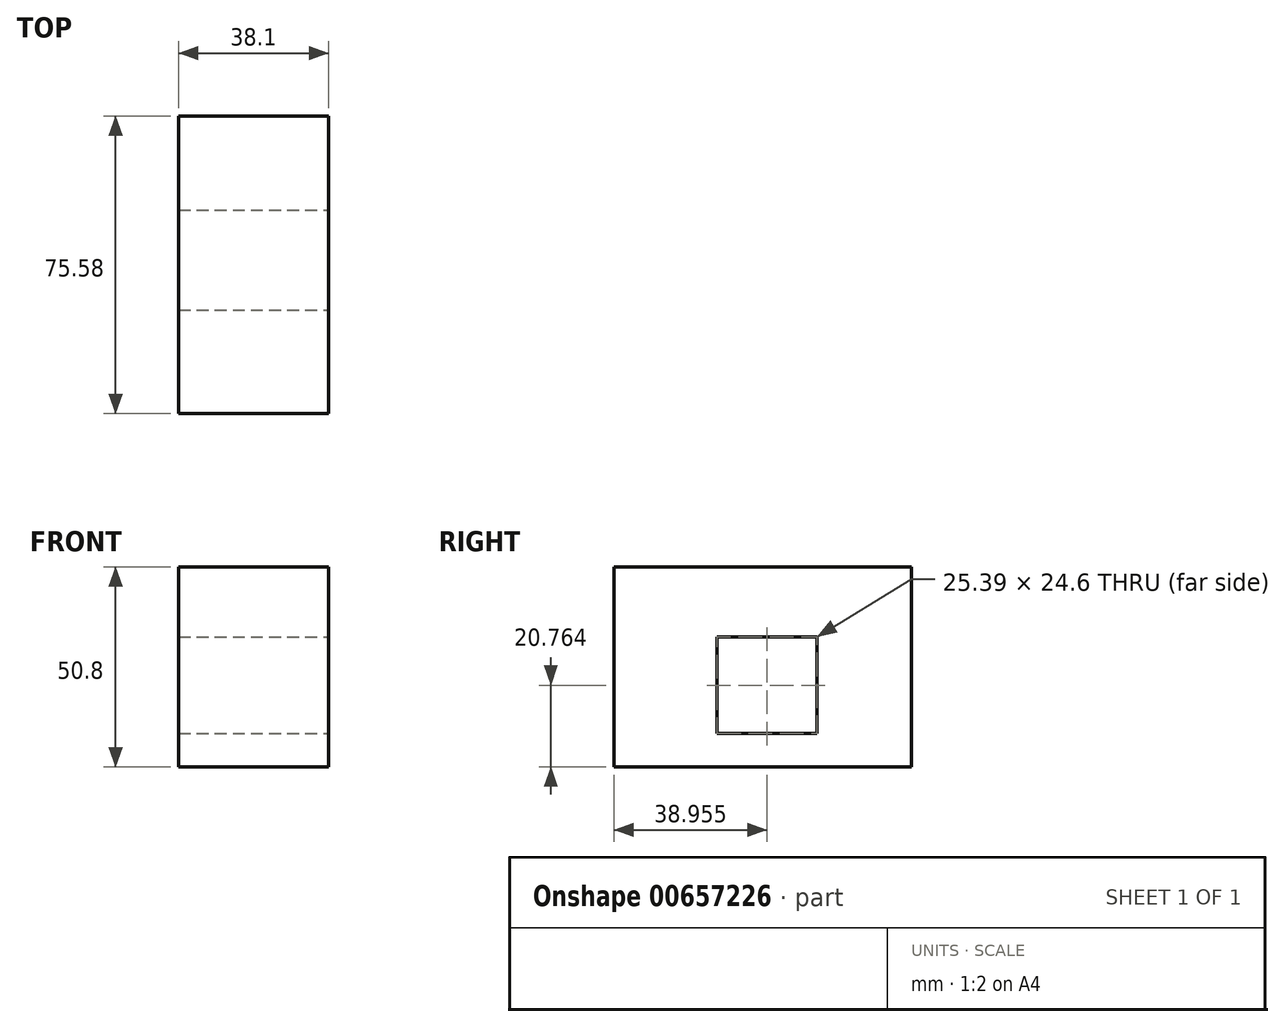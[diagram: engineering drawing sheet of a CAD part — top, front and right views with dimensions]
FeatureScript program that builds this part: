
annotation { "Feature Type Name" : "Feature", "Feature Type Description" : "" }
export const myFeature = defineFeature(function(context is Context, id is Id, definition is map)
    precondition{}
    {
        {
            var Q0;
            Q0=qCreatedBy(makeId("Top.planeOp"),FACE);
            var sketch = newSketch(context, id + "F0", { "sketchPlane" : qUnion([Q0])});
            skLineSegment(sketch, "E0.bottom", {"start": v(-45.74, -40.31) * mm, "end": v(-7.64, -40.31) * mm});
            skLineSegment(sketch, "E0.top", {"start": v(-45.74, 35.27) * mm, "end": v(-7.64, 35.27) * mm});
            skLineSegment(sketch, "E0.left", {"start": v(-45.74, -40.31) * mm, "end": v(-45.74, 35.27) * mm});
            skLineSegment(sketch, "E0.right", {"start": v(-7.64, -40.31) * mm, "end": v(-7.64, 35.27) * mm});
            skSolve(sketch);
        }
        {
            var Q0;
            Q0 = qSketchRegion(id + "F0", true);
            extrude(context, id + "F1", {"entities" : qUnion([Q0]), "depth" : 50.8 * mm, "offsetDistance" : 25.4 * mm});
        }
        {
            var Q0;
            Q0=makeQuery(id+"F1.opExtrude","SWEPT_FACE",FACE,{"disambiguationData":[OSD([sQuery(id+"F0.wireOp",EDGE,"E0.right")])]});
            var sketch = newSketch(context, id + "F2", { "sketchPlane" : qUnion([Q0])});
            skLineSegment(sketch, "E1.bottom", {"start": v(-14.05, 33.07) * mm, "end": v(11.34, 33.07) * mm});
            skLineSegment(sketch, "E1.top", {"start": v(-14.05, 8.46) * mm, "end": v(11.34, 8.46) * mm});
            skLineSegment(sketch, "E1.left", {"start": v(-14.05, 33.07) * mm, "end": v(-14.05, 8.46) * mm});
            skLineSegment(sketch, "E1.right", {"start": v(11.34, 33.07) * mm, "end": v(11.34, 8.46) * mm});
            skSolve(sketch);
        }
        {
            var Q0;
            Q0 = qSketchRegion(id + "F2", true);
            extrude(context, id + "F3", {"entities" : qUnion([Q0]), "operationType" : NewBodyOperationType.REMOVE, "oppositeDirection" : true, "depth" : 38.1 * mm, "offsetDistance" : 25.4 * mm});
        }
    });
